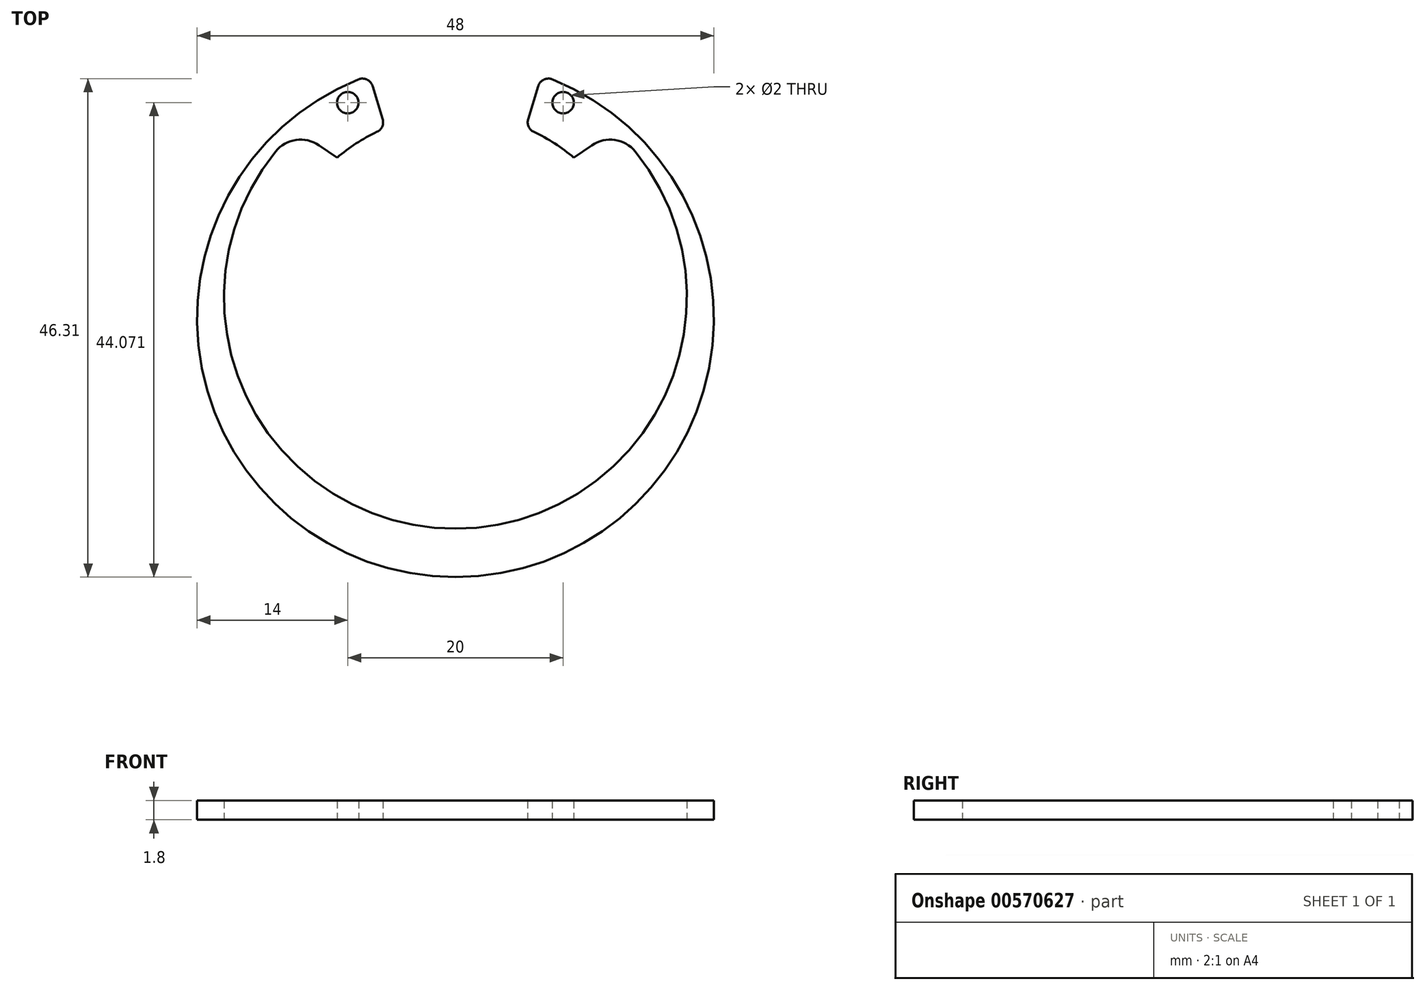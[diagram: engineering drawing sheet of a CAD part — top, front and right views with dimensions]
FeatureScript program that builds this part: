
annotation { "Feature Type Name" : "Feature", "Feature Type Description" : "" }
export const myFeature = defineFeature(function(context is Context, id is Id, definition is map)
    precondition{}
    {
        {
            var Q0;
            Q0=qCreatedBy(makeId("Top.planeOp"),FACE);
            var sketch = newSketch(context, id + "F0", { "sketchPlane" : qUnion([Q0])});
            skArc(sketch, "E0", {"start": v(-9.02, 22.24) * mm, "mid": v(0, -24) * mm, "end": v(9.02, 22.24) * mm});
            skLineSegment(sketch, "E1", {"start": v(27.76, 0) * mm, "end": v(-28.56, 0) * mm, "construction": true});
            skLineSegment(sketch, "E2", {"start": v(0, 29.13) * mm, "end": v(0, -29.45) * mm, "construction": true});
            skLineSegment(sketch, "E3.0", {"start": v(27.76, 2) * mm, "end": v(-28.56, 2) * mm, "construction": true});
            skArc(sketch, "E4", {"start": v(-16.7, 15.53) * mm, "mid": v(0, -19.5) * mm, "end": v(16.7, 15.53) * mm});
            skLineSegment(sketch, "E5", {"start": v(-7.69, 21.6) * mm, "end": v(-6.76, 18.55) * mm});
            skArc(sketch, "E6", {"start": v(-7.29, 17.36) * mm, "mid": v(-9.22, 16.28) * mm, "end": v(-11, 14.96) * mm});
            skLineSegment(sketch, "E7.MirrorCS", {"start": v(7.69, 21.6) * mm, "end": v(6.76, 18.55) * mm});
            skLineSegment(sketch, "E8", {"start": v(-11, 14.96) * mm, "end": v(-12.68, 16.11) * mm});
            skLineSegment(sketch, "E9.MirrorCS", {"start": v(11, 14.96) * mm, "end": v(12.68, 16.11) * mm});
            skArc(sketch, "E10.trimOffspring", {"start": v(11, 14.96) * mm, "mid": v(9.22, 16.28) * mm, "end": v(7.29, 17.36) * mm});
            skArc(sketch, "E11.filletArc", {"start": v(-12.68, 16.11) * mm, "mid": v(-14.8, 16.61) * mm, "end": v(-16.7, 15.53) * mm});
            skArc(sketch, "E12.filletArc", {"start": v(16.7, 15.53) * mm, "mid": v(14.8, 16.61) * mm, "end": v(12.68, 16.11) * mm});
            skPoint(sketch, "E13.visualSharp", {"position": v(-8, 22.63) * mm});
            skArc(sketch, "E13.filletArc", {"start": v(-7.69, 21.6) * mm, "mid": v(-8.21, 22.22) * mm, "end": v(-9.02, 22.24) * mm});
            skPoint(sketch, "E14.visualSharp", {"position": v(8, 22.63) * mm});
            skArc(sketch, "E14.filletArc", {"start": v(9.02, 22.24) * mm, "mid": v(8.21, 22.22) * mm, "end": v(7.69, 21.6) * mm});
            skPoint(sketch, "E15.visualSharp", {"position": v(6.5, 17.7) * mm});
            skArc(sketch, "E15.filletArc", {"start": v(6.76, 18.55) * mm, "mid": v(6.8, 17.86) * mm, "end": v(7.29, 17.36) * mm});
            skPoint(sketch, "E16.visualSharp", {"position": v(-6.5, 17.7) * mm});
            skArc(sketch, "E16.filletArc", {"start": v(-7.29, 17.36) * mm, "mid": v(-6.8, 17.86) * mm, "end": v(-6.76, 18.55) * mm});
            skCircle(sketch, "E17", {"center": v(-10, 20.07) * mm, "radius": 1 * mm});
            skCircle(sketch, "E18.MirrorC", {"center": v(10, 20.07) * mm, "radius": 1 * mm});
            skSolve(sketch);
        }
        {
            var Q0;
            Q0=makeQuery(id+"F0.imprint","IMPRINT",FACE,{"disambiguationData":[TD([[makeQuery(id+"F0.imprint","IMPRINT",EDGE,{"derivedFrom":sQuery(id+"F0.wireOp",EDGE,"E4")}),-1.0]])]});
            extrude(context, id + "F1", {"entities" : qUnion([Q0]), "depth" : 1.8 * mm, "offsetDistance" : 25 * mm});
        }
    });
